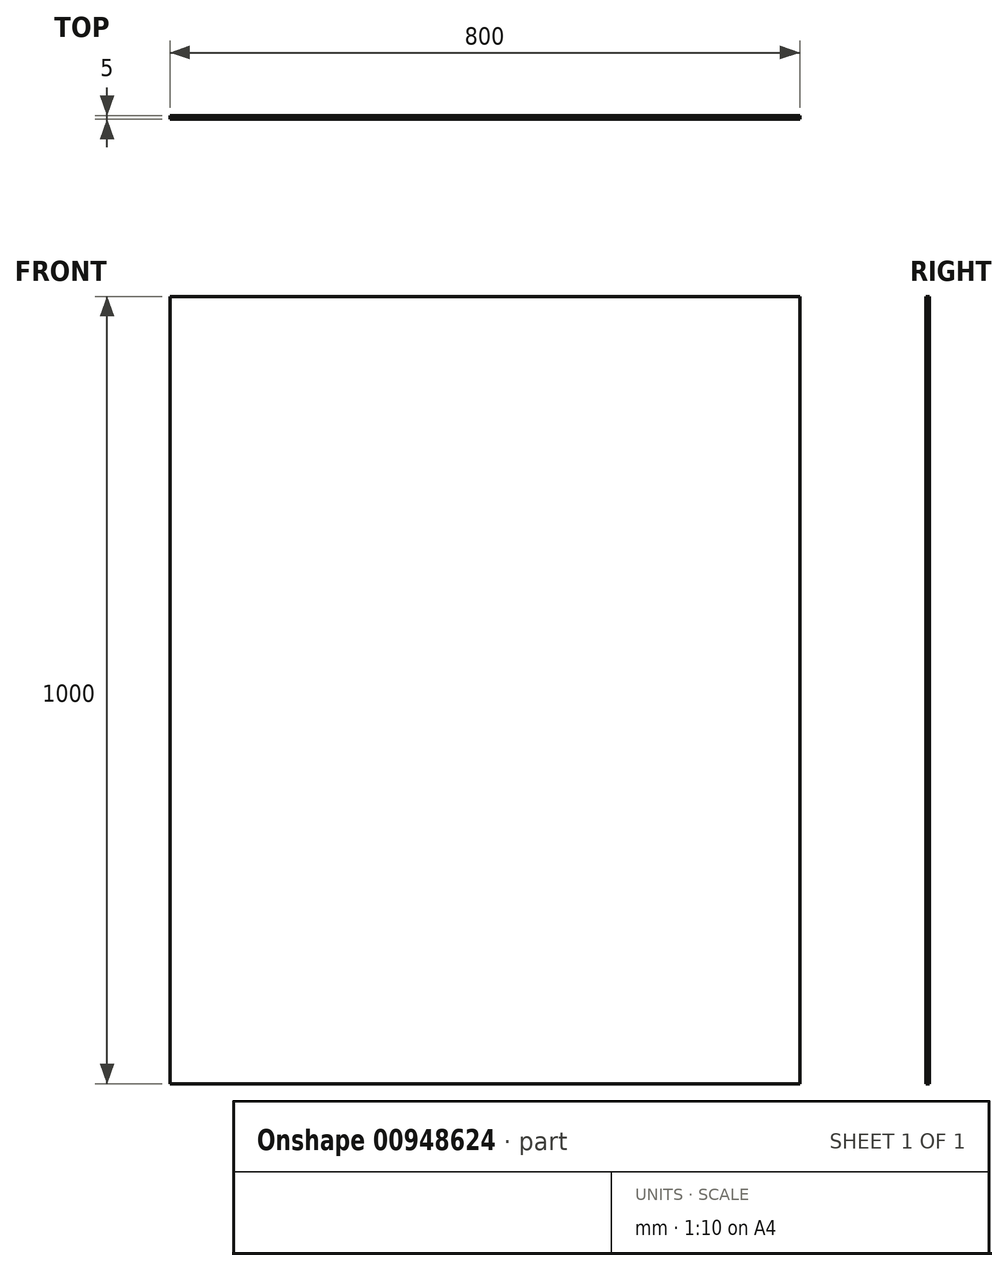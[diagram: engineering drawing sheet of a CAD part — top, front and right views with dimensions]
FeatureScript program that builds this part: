
annotation { "Feature Type Name" : "Feature", "Feature Type Description" : "" }
export const myFeature = defineFeature(function(context is Context, id is Id, definition is map)
    precondition{}
    {
        {
            var Q0;
            Q0=qCreatedBy(makeId("Front.planeOp"),FACE);
            var sketch = newSketch(context, id + "F0", { "sketchPlane" : qUnion([Q0])});
            skLineSegment(sketch, "E0.bottom", {"start": v(0, 0) * mm, "end": v(800, 0) * mm});
            skLineSegment(sketch, "E0.top", {"start": v(0, 1000) * mm, "end": v(800, 1000) * mm});
            skLineSegment(sketch, "E0.left", {"start": v(0, 0) * mm, "end": v(0, 1000) * mm});
            skLineSegment(sketch, "E0.right", {"start": v(800, 0) * mm, "end": v(800, 1000) * mm});
            skSolve(sketch);
        }
        {
            var Q0;
            Q0 = qSketchRegion(id + "F0", true);
            extrude(context, id + "F1", {"entities" : qUnion([Q0]), "depth" : 5 * mm, "offsetDistance" : 25 * mm});
        }
    });
